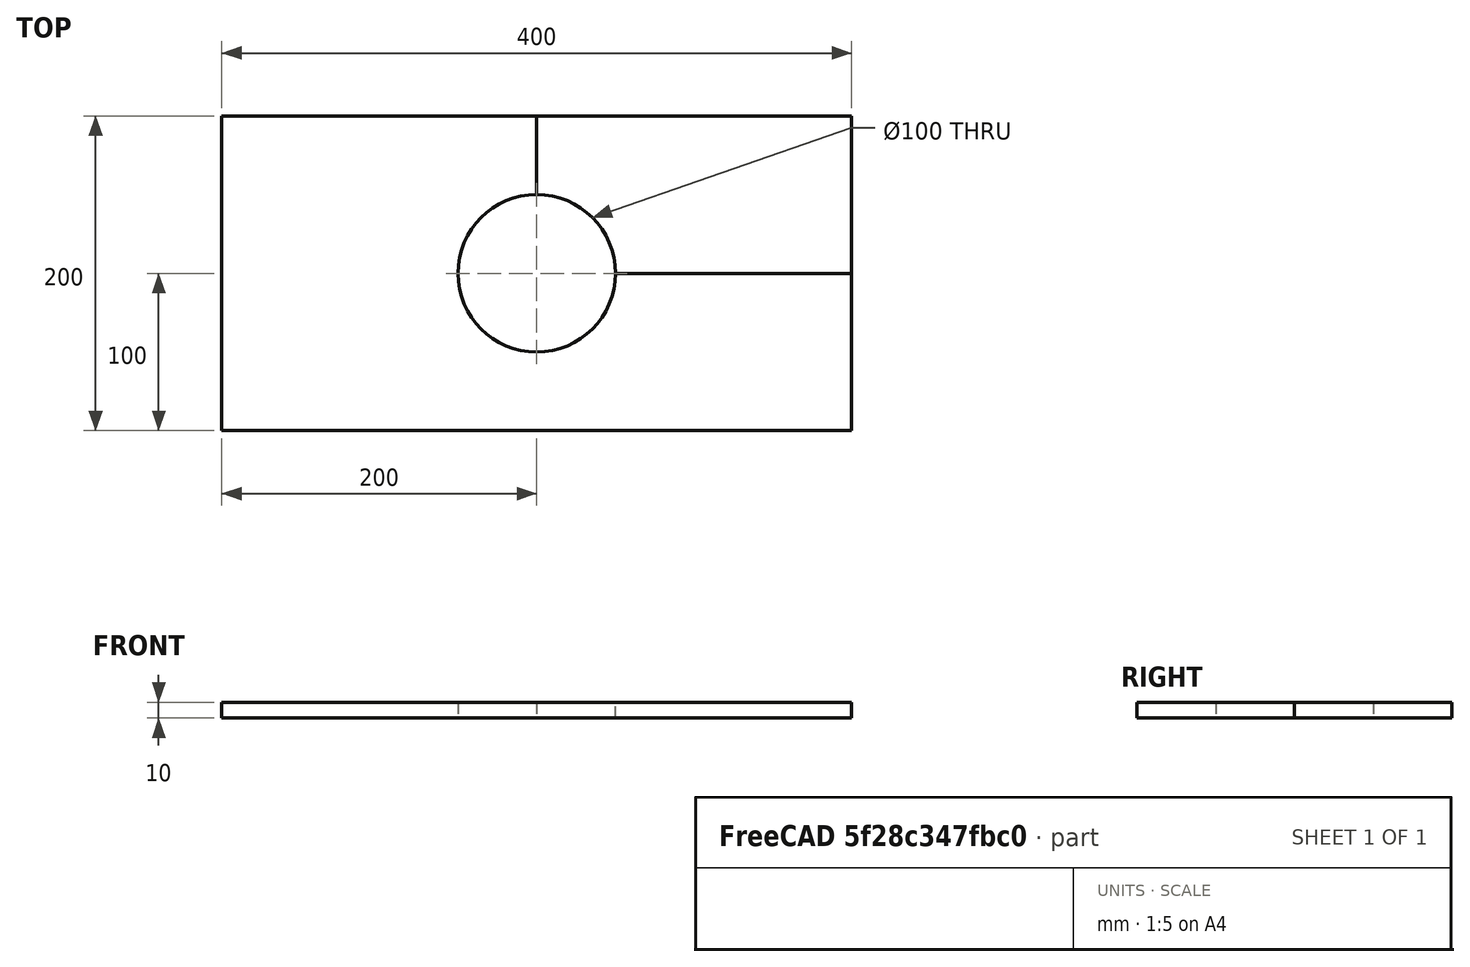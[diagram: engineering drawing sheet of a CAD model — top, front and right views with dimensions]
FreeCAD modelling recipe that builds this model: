
FCSTD DOCUMENT  (FreeCAD 0.21R33771 (Git))
Label: Plate_with_hole_Example
License: All rights reserved
LicenseURL: http://en.wikipedia.org/wiki/All_rights_reserved
objects: Fem::ConstraintDisplacement×3, Part::Box×2, Part::Cylinder×2, Part::Cut×2, Fem::ConstraintPressure×1, App::MaterialObjectPython×1, Fem::FemSolverObjectPython×1, Fem::FemMeshObjectPython×1, Fem::FemAnalysis×1
note: 6 computed .brp shape members not serialized (recipe doc carries the construction recipe); baked Part::Feature solids carry a one-line shape summary decoded from their .brp

FEATURE [Part::Box] Box  label="Cube"
  AttacherType = Attacher::AttachEngine3D
  Height = 10
  Length = 200
  Width = 100
FEATURE [Part::Cylinder] Cylinder
  Angle = 360
  AttacherType = Attacher::AttachEngine3D
  FirstAngle = 0
  Height = 10
  Radius = 50
  SecondAngle = 0
FEATURE [Part::Cut] Cut
  Base = -> Box
  Tool = -> Cylinder
FEATURE [Fem::ConstraintDisplacement] FemConstraintDisplacement
  NormalDirection = (-1,0,0)
  Normals = (12) [(-1,0,0),(-1,0,0),(-1,0,0),(-1,0,0),(-1,0,0),(-1,0,0),(-1,0,0),(-1,0,0),(-1,0,0),(-1,0,0),(-1,0,0),(-1,0,0)]
  Points = (12) [(0,100,0),(0,100,5),(0,100,10),(0,83.3333,0),(0,83.3333,5),(0,83.3333,10),(0,66.6667,0),(0,66.6667,5),(0,66.6667,10),(0,50,0),(0,50,5),(0,50,10)]
  References = -> [Cut]
  hasXFormula = false
  hasYFormula = false
  hasZFormula = false
  rotxFix = false
  rotxFree = true
  rotyFix = false
  rotyFree = true
  rotzFix = false
  rotzFree = true
  useFlowSurfaceForce = false
  xDisplacement = 0
  xFix = false
  xFree = false
  xRotation = 0
  yDisplacement = 0
  yFix = false
  yFree = true
  yRotation = 0
  zDisplacement = 0
  zFix = false
  zFree = true
  zRotation = 0
FEATURE [Fem::ConstraintDisplacement] FemConstraintDisplacement001
  NormalDirection = (1,0,0)
  Normals = (12) [(1,0,0),(1,0,0),(1,0,0),(1,0,0),(1,0,0),(1,0,0),(1,0,0),(1,0,0),(1,0,0),(1,0,0),(1,0,0),(1,0,0)]
  Points = (12) [(200,100,0),(200,100,5),(200,100,10),(200,66.6667,0),(200,66.6667,5),(200,66.6667,10),(200,33.3333,0),(200,33.3333,5),(200,33.3333,10),(200,0,0),(200,0,5),(200,0,10)]
  References = -> [Cut]
  hasXFormula = false
  hasYFormula = false
  hasZFormula = false
  rotxFix = false
  rotxFree = true
  rotyFix = false
  rotyFree = true
  rotzFix = false
  rotzFree = true
  useFlowSurfaceForce = false
  xDisplacement = 0
  xFix = false
  xFree = true
  xRotation = 0
  yDisplacement = 0
  yFix = false
  yFree = false
  yRotation = 0
  zDisplacement = 0
  zFix = false
  zFree = true
  zRotation = 0
FEATURE [Fem::ConstraintPressure] FemConstraintPressure
  NormalDirection = (1,0,0)
  Normals = (12) [(1,0,0),(1,0,0),(1,0,0),(1,0,0),(1,0,0),(1,0,0),(1,0,0),(1,0,0),(1,0,0),(1,0,0),(1,0,0),(1,0,0)]
  Points = (12) [(200,100,0),(200,100,5),(200,100,10),(200,66.6667,0),(200,66.6667,5),(200,66.6667,10),(200,33.3333,0),(200,33.3333,5),(200,33.3333,10),(200,0,0),(200,0,5),(200,0,10)]
  Pressure = 100
  References = -> [Cut]
  Reversed = true
FEATURE [App::MaterialObjectPython] SolidMaterial  # material (typed FeaturePython)
  Category = 0
  Material = AuthorAndLicense=(c) 2013 Juergen Riegel (CC-BY 3.0); CardName=CalculiX-Steel; Density=7900 kg/m^3; Description=Standard steel material for CalculiX sample calculations; Father=Metal; Name=CalculiX-Steel; PoissonRatio=0.3; SpecificHeat=590 J/kg/K; ThermalConductivity=43 W/m/K; ThermalExpansionCoefficient=0.000012 m/m/K; YoungsModulus=210000 MPa
FEATURE [Fem::ConstraintDisplacement] FemConstraintDisplacement002
  NormalDirection = (0,0,-1)
  Normals = (3) [(0,0,-1),(0,0,-1),(0,0,-1)]
  Points = (3) [(-1.053e-12,50,10),(-1.053e-12,50,0),(50,-1.2e-14,0)]
  References = -> [Cut]
  Scale = 15
  hasXFormula = false
  hasYFormula = false
  hasZFormula = false
  rotxFix = false
  rotxFree = true
  rotyFix = false
  rotyFree = true
  rotzFix = false
  rotzFree = true
  useFlowSurfaceForce = false
  xDisplacement = 0
  xFix = false
  xFree = true
  xRotation = 0
  yDisplacement = 0
  yFix = false
  yFree = true
  yRotation = 0
  zDisplacement = 0
  zFix = false
  zFree = false
  zRotation = 0
FEATURE [Fem::FemSolverObjectPython] SolverCcxTools  # FEM object (typed FeaturePython)
  AnalysisType = 0
  BeamReducedIntegration = true
  BeamShellResultOutput3D = false
  BucklingFactors = 1
  EigenmodeHighLimit = 1000000
  EigenmodeLowLimit = 0
  EigenmodesCount = 10
  GeometricalNonlinearity = 1
  IterationsControlParameterCutb = 0.25,0.5,0.75,0.85,,,1.5,
  IterationsControlParameterIter = 4,8,9,200,10,400,,200,,
  IterationsControlParameterTimeUse = false
  IterationsMaximum = 200
  IterationsThermoMechMaximum = 2000
  IterationsUserDefinedIncrementations = false
  IterationsUserDefinedTimeStepLength = false
  MaterialNonlinearity = 1
  MatrixSolverType = 0
  ModelSpace = 0
  OutputFrequency = 1
  SplitInputWriter = false
  ThermoMechSteadyState = true
  ThermoMechType = 0
  TimeEnd = 1
  TimeInitialStep = 1
  TimeMaximumStep = 1
  TimeMinimumStep = 1e-05
FEATURE [Part::Box] Box001  label="Cube001"
  AttacherType = Attacher::AttachEngine3D
  Height = 10
  Length = 400
  Placement = pos=(-200,-100,0) rot=(0,0,1;0rad)
  Width = 200
FEATURE [Part::Cylinder] Cylinder001
  Angle = 360
  AttacherType = Attacher::AttachEngine3D
  FirstAngle = 0
  Height = 10
  Radius = 50
  SecondAngle = 0
FEATURE [Part::Cut] Cut001
  Base = -> Box001
  Tool = -> Cylinder001
FEATURE [Fem::FemMeshObjectPython] FEMMeshGmsh  # FEM object (typed FeaturePython)
  Algorithm2D = 0
  Algorithm3D = 0
  CharacteristicLengthMax = 0
  CharacteristicLengthMin = 0
  CoherenceMesh = true
  ElementDimension = 0
  ElementOrder = 1
  GeometryTolerance = 1e-06
  GroupsOfNodes = false
  HighOrderOptimize = 0
  MeshSizeFromCurvature = 12
  OptimizeNetgen = false
  OptimizeStd = true
  Part = -> Cut
  RecombinationAlgorithm = 0
  Recombine3DAll = false
  RecombineAll = false
  SecondOrderLinear = false
FEATURE [Fem::FemAnalysis] Analysis
  Group = -> [SolverCcxTools,FemConstraintDisplacement,FemConstraintDisplacement001,FemConstraintPressure,SolidMaterial,FemConstraintDisplacement002,FEMMeshGmsh]
